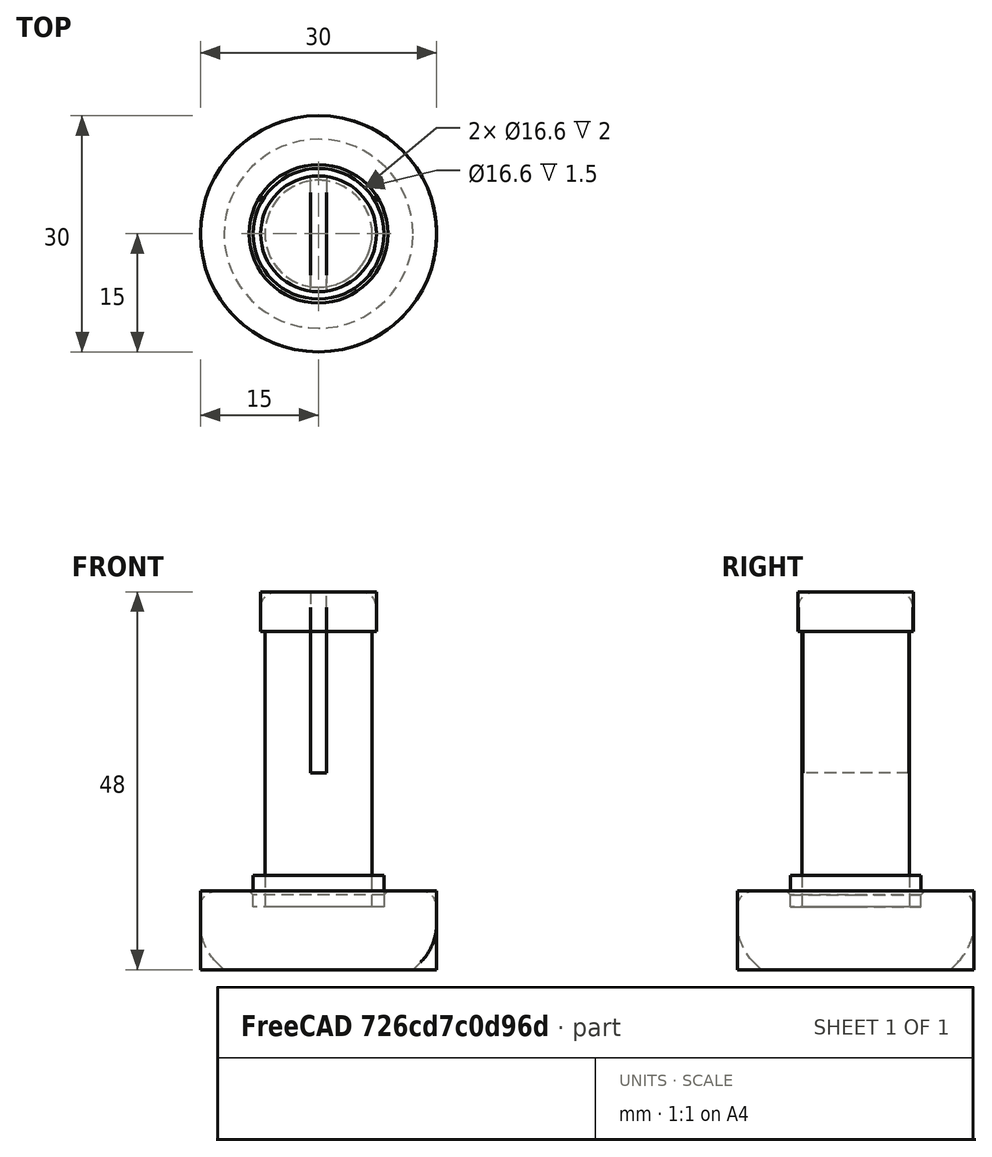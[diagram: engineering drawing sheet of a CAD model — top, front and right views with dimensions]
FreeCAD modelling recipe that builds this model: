
FCSTD DOCUMENT  (FreeCAD 0.16R)
Label: Barplugs_5-8
License: All rights reserved
LicenseURL: http://en.wikipedia.org/wiki/All_rights_reserved
objects: Sketcher::SketchObject×6, PartDesign::Pad×3, PartDesign::Fillet×3, PartDesign::Pocket×2, PartDesign::Chamfer×2, Mesh::Feature×1
note: 21 computed .brp shape members not serialized (recipe doc carries the construction recipe); baked Part::Feature solids carry a one-line shape summary decoded from their .brp

FEATURE [Sketcher::SketchObject] Sketch001
  Placement = pos=(0,0,0) rot=(1,0,0;3.14159rad)
  sketch-geometry (1):
    g0: Circle CenterX=0 CenterY=0 CenterZ=0 NormalX=0 NormalY=0 NormalZ=1 Radius=15
  constraints (2):
    c: Radius(g0) = 15
    c: Coincident(g0,g-1)
FEATURE [Sketcher::SketchObject] Sketch002
FEATURE [PartDesign::Pad] Pad
  Length = 10
  Length2 = 100
  Placement = pos=(0,0,0) rot=(1,0,0;3.14159rad)
  Sketch = -> Sketch001
  Type = 0
FEATURE [Sketcher::SketchObject] Sketch003
  Support = -> Pad [Face2]
  sketch-geometry (1):
    g0: Circle CenterX=0 CenterY=0 CenterZ=0 NormalX=0 NormalY=0 NormalZ=1 Radius=8.3
  constraints (2):
    c: Radius(g0) = 8.3
    c: Coincident(g0,g-1)
FEATURE [PartDesign::Pocket] Pocket
  Length = 2
  Placement = pos=(0,0,0) rot=(1,0,0;3.14159rad)
  Sketch = -> Sketch003
  Type = 0
FEATURE [Sketcher::SketchObject] Sketch
  Placement = pos=(0,0,-2) rot=(0,0,1;0rad)
  Support = -> Pocket [Face5]
  sketch-geometry (1):
    g0: Circle CenterX=0 CenterY=0 CenterZ=0 NormalX=0 NormalY=0 NormalZ=1 Radius=6.8
  constraints (2):
    c: Radius(g0) = 6.8
    c: Coincident(g0,g-1)
FEATURE [PartDesign::Pad] Pad001
  Length = 35
  Length2 = 100
  Placement = pos=(0,0,0) rot=(1,0,0;3.14159rad)
  Sketch = -> Sketch
  Type = 0
FEATURE [Sketcher::SketchObject] Sketch004
  Placement = pos=(0,0,33) rot=(0,0,1;0rad)
  Support = -> Pad001 [Face7]
  sketch-geometry (1):
    g0: Circle CenterX=0 CenterY=0 CenterZ=0 NormalX=0 NormalY=0 NormalZ=1 Radius=7.35
  constraints (2):
    c: Radius(g0) = 7.35
    c: Coincident(g0,g-1)
FEATURE [PartDesign::Pad] Pad002
  Length = 5
  Length2 = 100
  Placement = pos=(0,0,0) rot=(1,0,0;3.14159rad)
  Sketch = -> Sketch004
  Type = 0
FEATURE [Sketcher::SketchObject] Sketch005
  Placement = pos=(0,0,38) rot=(0,0,1;0rad)
  Support = -> Pad002 [Face9]
  sketch-geometry (4):
    g0: LineSegment StartX=-1 StartY=10 StartZ=0 EndX=1 EndY=10 EndZ=0
    g1: LineSegment StartX=1 StartY=10 StartZ=0 EndX=1 EndY=-10 EndZ=0
    g2: LineSegment StartX=1 StartY=-10 StartZ=0 EndX=-1 EndY=-10 EndZ=0
    g3: LineSegment StartX=-1 StartY=-10 StartZ=0 EndX=-1 EndY=10 EndZ=0
  constraints (12):
    c: Coincident(g0,g1)
    c: Coincident(g1,g2)
    c: Coincident(g2,g3)
    c: Coincident(g3,g0)
    c: Horizontal(g0)
    c: Horizontal(g2)
    c: Vertical(g1)
    c: Vertical(g3)
    c: Symmetric(g1,g2,g-2)
    c: Distance(g0) = 2
    c: Symmetric(g0,g1,g-1)
    c: Distance(g1) = 20
FEATURE [PartDesign::Pocket] Pocket001
  Length = 23
  Placement = pos=(0,0,0) rot=(1,0,0;3.14159rad)
  Sketch = -> Sketch005
  Type = 0
FEATURE [PartDesign::Fillet] Fillet
  Base = -> Pocket001 [Edge35,Edge36]
  Placement = pos=(0,0,0) rot=(1,0,0;3.14159rad)
  Radius = 2
FEATURE [PartDesign::Chamfer] Chamfer
  Base = -> Fillet [Edge44]
  Placement = pos=(0,0,0) rot=(1,0,0;3.14159rad)
  Size = 3
FEATURE [PartDesign::Fillet] Fillet001
  Base = -> Chamfer [Edge2]
  Placement = pos=(0,0,0) rot=(1,0,0;3.14159rad)
  Radius = 7
FEATURE [PartDesign::Fillet] Fillet002
  Base = -> Fillet001 [Edge3]
  Placement = pos=(0,0,0) rot=(1,0,0;3.14159rad)
  Radius = 2
FEATURE [PartDesign::Chamfer] Chamfer001
  Base = -> Fillet002 [Edge8]
  Placement = pos=(0,0,0) rot=(1,0,0;3.14159rad)
  Size = 0.5
FEATURE [Mesh::Feature] Mesh  label="Chamfer001 (Meshed)"
